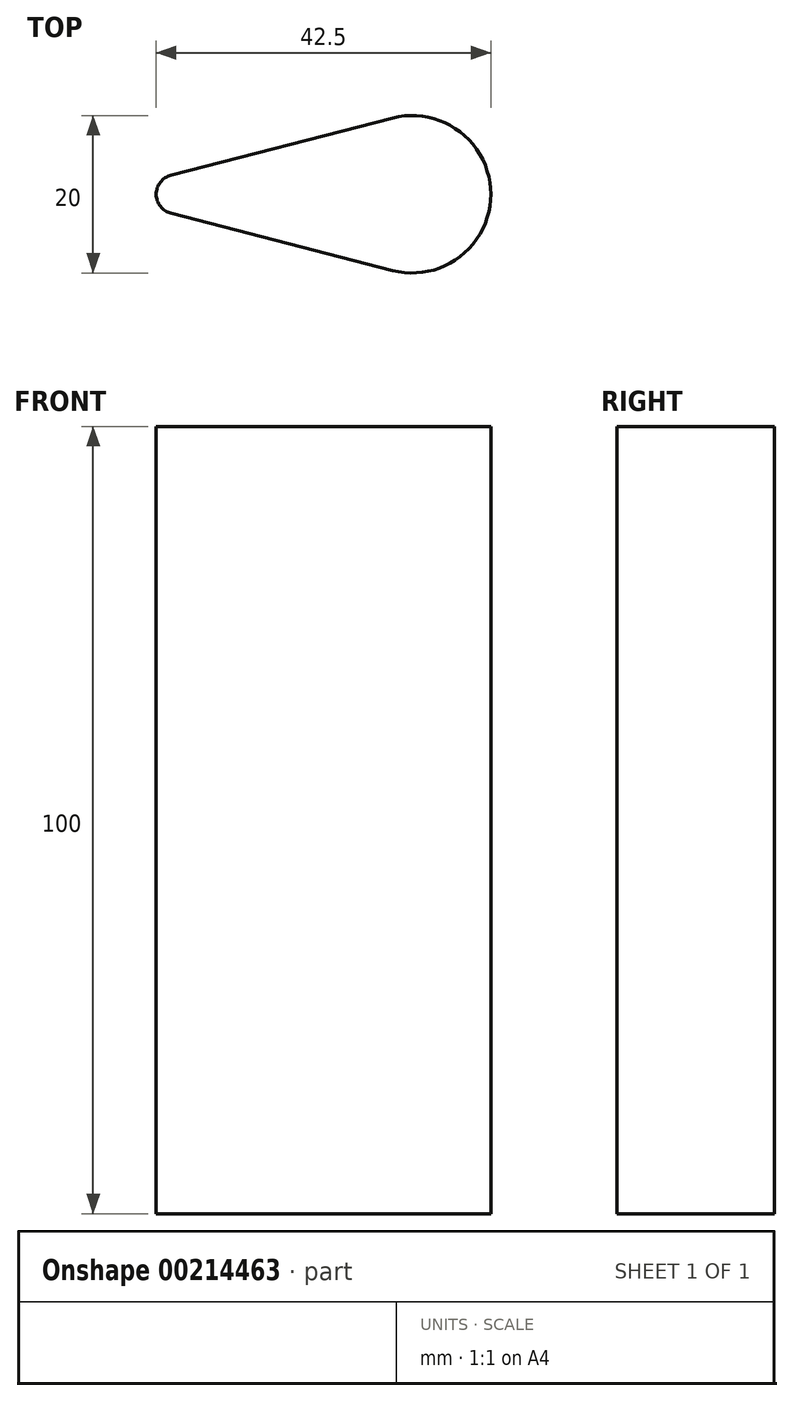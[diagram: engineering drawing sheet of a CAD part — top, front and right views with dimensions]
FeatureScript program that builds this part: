
annotation { "Feature Type Name" : "Feature", "Feature Type Description" : "" }
export const myFeature = defineFeature(function(context is Context, id is Id, definition is map)
    precondition{}
    {
        {
            var Q0;
            Q0=qCreatedBy(makeId("Top.planeOp"),FACE);
            var sketch = newSketch(context, id + "F0", { "sketchPlane" : qUnion([Q0])});
            skCircle(sketch, "E0", {"center": v(-10, 0) * mm, "radius": 2.5 * mm});
            skCircle(sketch, "E1", {"center": v(20, 0) * mm, "radius": 10 * mm});
            skLineSegment(sketch, "E2", {"start": v(-10.62, 2.42) * mm, "end": v(17.5, 9.68) * mm});
            skLineSegment(sketch, "E3", {"start": v(-10.62, -2.42) * mm, "end": v(17.5, -9.68) * mm});
            skSolve(sketch);
        }
        {
            var Q0;
            {var subQ0=sQuery(id+"F0.wireOp",EDGE,"E2");Q0=makeQuery(id+"F0.imprint","IMPRINT",FACE,{"disambiguationData":[TD([[makeQuery(id+"F0.imprint","IMPRINT",EDGE,{"derivedFrom":subQ0}),-1.0]])]});}
            var Q1;
            {var subQ0=sQuery(id+"F0.wireOp",EDGE,"E1");var subQ1=makeQuery(id+"F0.imprint","INTERSECT",VERTEX,{"derivedFrom":[subQ0,sQuery(id+"F0.wireOp",EDGE,"E2")]});Q1=makeQuery(id+"F0.imprint","IMPRINT",FACE,{"disambiguationData":[TD([[makeQuery(id+"F0.imprint","IMPRINT",EDGE,{"disambiguationData":[TD([[subQ1,-1.0]])],"derivedFrom":subQ0}),1.0]])]});}
            var Q2;
            {var subQ0=sQuery(id+"F0.wireOp",EDGE,"E0");var subQ1=makeQuery(id+"F0.imprint","INTERSECT",VERTEX,{"derivedFrom":[subQ0,sQuery(id+"F0.wireOp",EDGE,"E2")]});Q2=makeQuery(id+"F0.imprint","IMPRINT",FACE,{"disambiguationData":[TD([[makeQuery(id+"F0.imprint","IMPRINT",EDGE,{"disambiguationData":[TD([[subQ1,-1.0]])],"derivedFrom":subQ0}),1.0]])]});}
            extrude(context, id + "F1", {"entities" : qUnion([Q0, Q1, Q2]), "depth" : 100 * mm});
        }
    });
